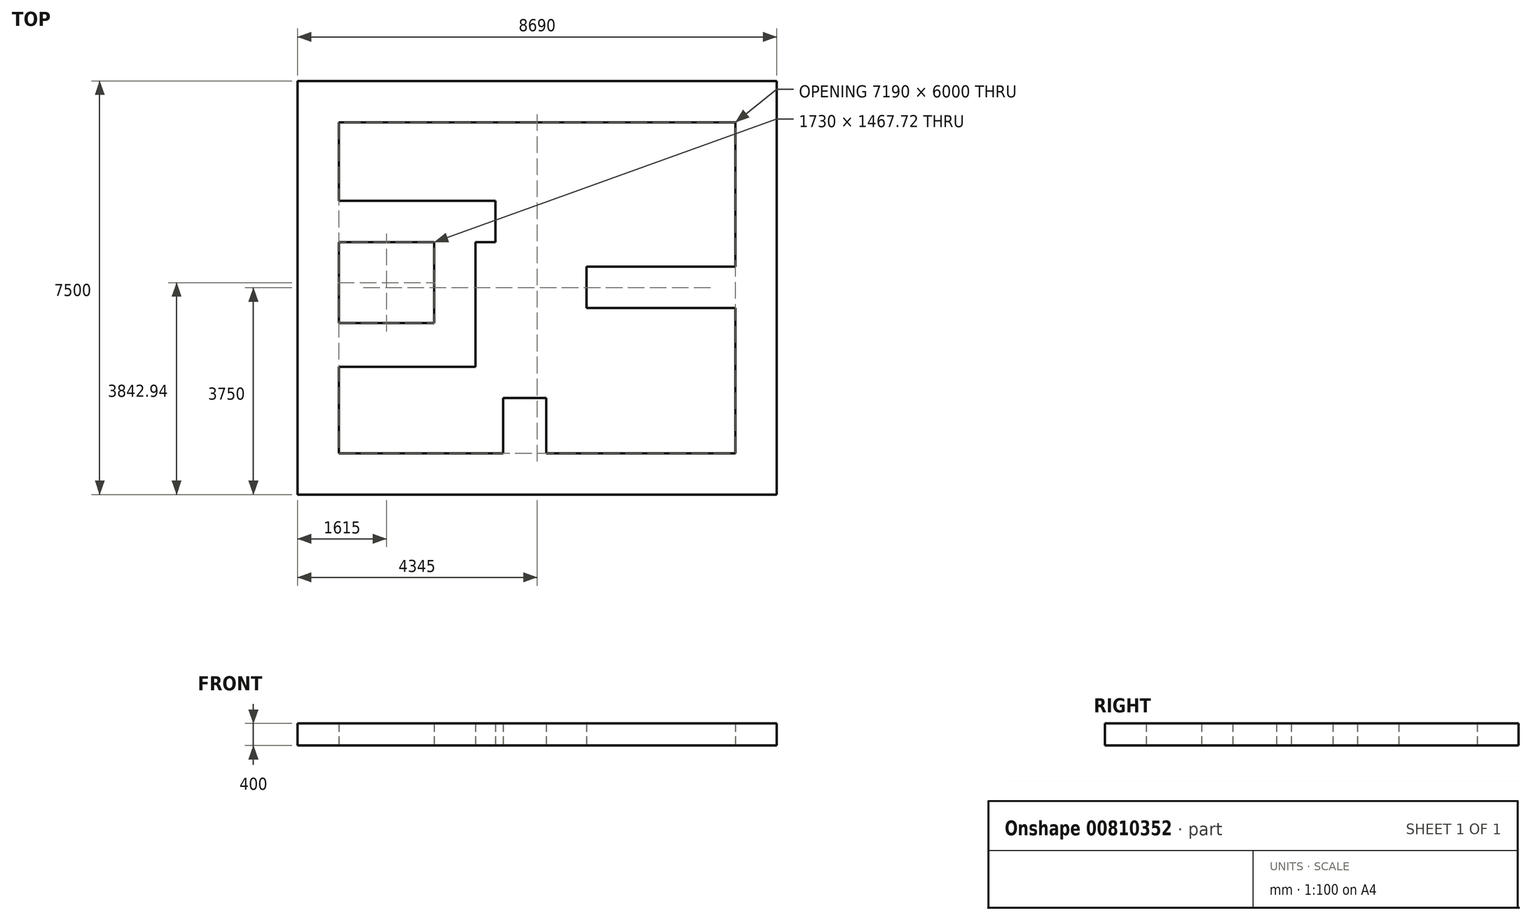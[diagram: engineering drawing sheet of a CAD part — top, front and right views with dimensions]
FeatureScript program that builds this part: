
annotation { "Feature Type Name" : "Feature", "Feature Type Description" : "" }
export const myFeature = defineFeature(function(context is Context, id is Id, definition is map)
    precondition{}
    {
        {
            var Q0;
            Q0=qCreatedBy(makeId("Top.planeOp"),FACE);
            var sketch = newSketch(context, id + "F0", { "sketchPlane" : qUnion([Q0])});
            skLineSegment(sketch, "E0.bottom", {"start": v(0, 0) * mm, "end": v(8690, 0) * mm});
            skLineSegment(sketch, "E0.top", {"start": v(0, 7500) * mm, "end": v(8690, 7500) * mm});
            skLineSegment(sketch, "E0.left", {"start": v(0, 0) * mm, "end": v(0, 7500) * mm});
            skLineSegment(sketch, "E0.right", {"start": v(8690, 0) * mm, "end": v(8690, 7500) * mm});
            skLineSegment(sketch, "E1", {"start": v(750, 750) * mm, "end": v(3728.67, 750) * mm});
            skLineSegment(sketch, "E2", {"start": v(3728.67, 750) * mm, "end": v(3728.67, 1750) * mm});
            skLineSegment(sketch, "E3", {"start": v(3728.67, 1750) * mm, "end": v(4508.67, 1750) * mm});
            skLineSegment(sketch, "E4", {"start": v(4508.67, 1750) * mm, "end": v(4508.67, 750) * mm});
            skLineSegment(sketch, "E5", {"start": v(4508.67, 750) * mm, "end": v(7940, 750) * mm});
            skLineSegment(sketch, "E6", {"start": v(7940, 750) * mm, "end": v(7940, 3381.54) * mm});
            skLineSegment(sketch, "E7", {"start": v(7940, 3381.54) * mm, "end": v(5240, 3381.54) * mm});
            skLineSegment(sketch, "E8", {"start": v(5240, 3381.54) * mm, "end": v(5240, 4131.54) * mm});
            skLineSegment(sketch, "E9", {"start": v(5240, 4131.54) * mm, "end": v(7940, 4131.54) * mm});
            skLineSegment(sketch, "E10", {"start": v(7940, 4131.54) * mm, "end": v(7940, 6750) * mm});
            skLineSegment(sketch, "E11", {"start": v(7940, 6750) * mm, "end": v(750, 6750) * mm});
            skLineSegment(sketch, "E12", {"start": v(750, 6750) * mm, "end": v(750, 5326.8) * mm});
            skLineSegment(sketch, "E13", {"start": v(750, 5326.8) * mm, "end": v(3590, 5326.8) * mm});
            skLineSegment(sketch, "E14", {"start": v(3590, 5326.8) * mm, "end": v(3590, 4576.8) * mm});
            skLineSegment(sketch, "E15", {"start": v(3590, 4576.8) * mm, "end": v(3230, 4576.8) * mm});
            skLineSegment(sketch, "E16", {"start": v(3230, 4576.8) * mm, "end": v(3230, 2319.08) * mm});
            skLineSegment(sketch, "E17", {"start": v(3230, 2319.08) * mm, "end": v(750, 2319.08) * mm});
            skLineSegment(sketch, "E18", {"start": v(750, 2319.08) * mm, "end": v(750, 750) * mm});
            skLineSegment(sketch, "E19", {"start": v(750, 4576.8) * mm, "end": v(2480, 4576.8) * mm});
            skLineSegment(sketch, "E20", {"start": v(2480, 4576.8) * mm, "end": v(2480, 3109.08) * mm});
            skLineSegment(sketch, "E21", {"start": v(2480, 3109.08) * mm, "end": v(750, 3109.08) * mm});
            skLineSegment(sketch, "E22", {"start": v(750, 3109.08) * mm, "end": v(750, 4576.8) * mm});
            skSolve(sketch);
        }
        {
            var Q0;
            Q0=makeQuery(id+"F0.imprint","IMPRINT",FACE,{"disambiguationData":[TD([[makeQuery(id+"F0.imprint","IMPRINT",EDGE,{"derivedFrom":sQuery(id+"F0.wireOp",EDGE,"E0.bottom")}),1.0]])]});
            extrude(context, id + "F1", {"entities" : qUnion([Q0]), "depth" : 400 * mm, "offsetDistance" : 25 * mm});
        }
    });
